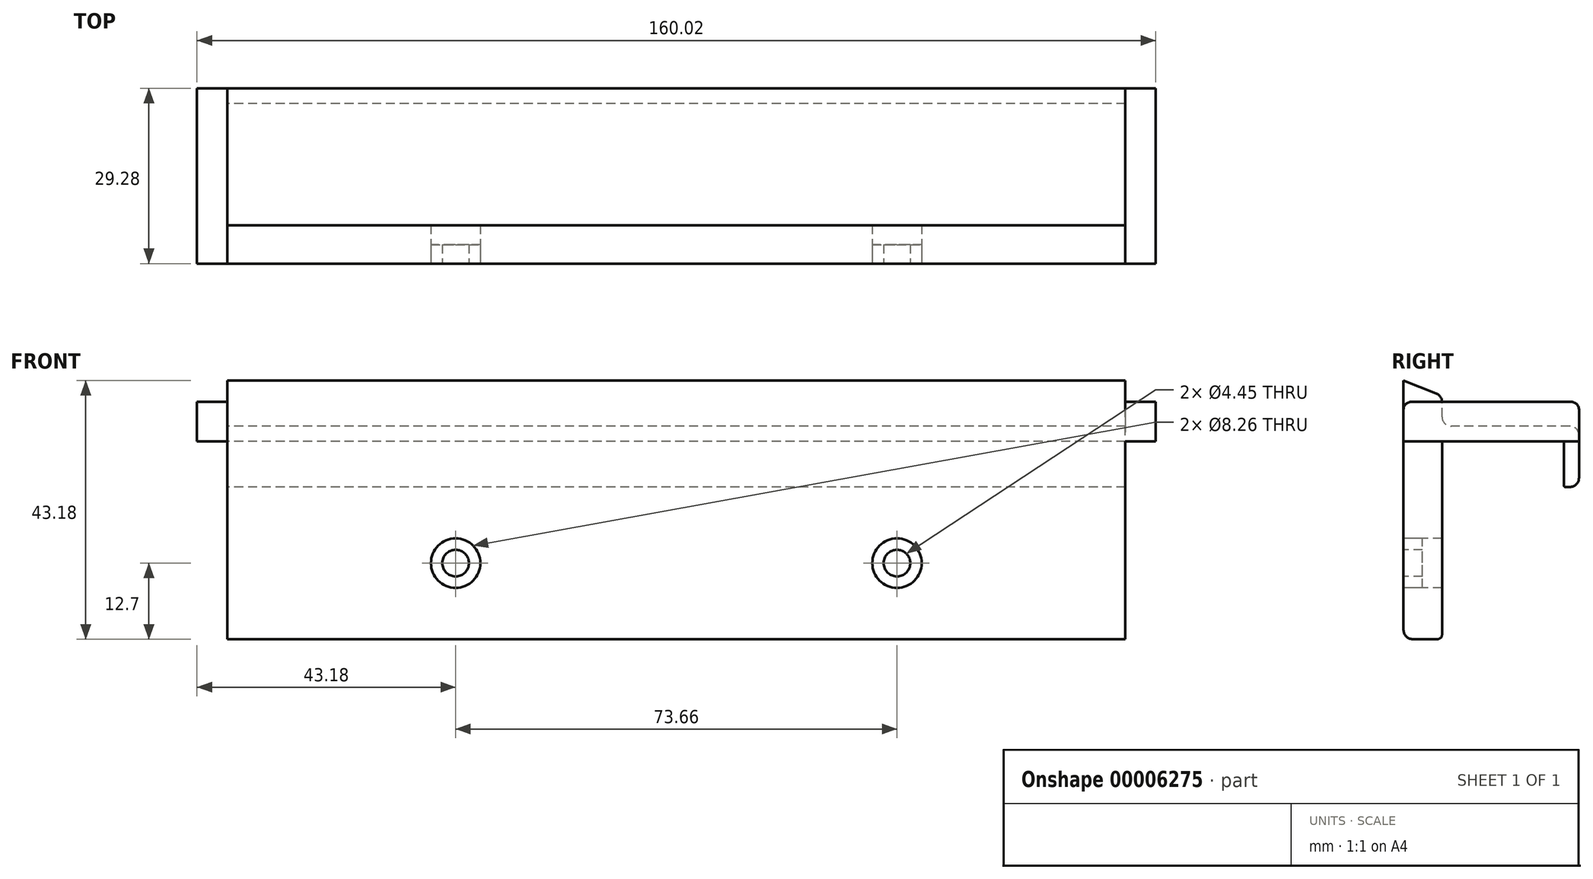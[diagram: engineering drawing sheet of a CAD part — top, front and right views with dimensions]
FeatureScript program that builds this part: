
annotation { "Feature Type Name" : "Feature", "Feature Type Description" : "" }
export const myFeature = defineFeature(function(context is Context, id is Id, definition is map)
    precondition{}
    {
        {
            var Q0;
            Q0=qCreatedBy(makeId("Right.planeOp"),FACE);
            var sketch = newSketch(context, id + "F0", { "sketchPlane" : qUnion([Q0])});
            skLineSegment(sketch, "E0", {"start": v(0.25, 0) * mm, "end": v(20.07, 0) * mm});
            skLineSegment(sketch, "E1", {"start": v(20.32, -0.25) * mm, "end": v(20.32, -7.37) * mm});
            skLineSegment(sketch, "E2", {"start": v(20.57, -7.62) * mm, "end": v(21.34, -7.62) * mm});
            skLineSegment(sketch, "E3", {"start": v(22.86, -6.1) * mm, "end": v(22.86, 1.02) * mm});
            skLineSegment(sketch, "E4", {"start": v(21.34, 2.54) * mm, "end": v(1.52, 2.54) * mm});
            skLineSegment(sketch, "E5", {"start": v(0, 4.06) * mm, "end": v(0, 6.58) * mm});
            skLineSegment(sketch, "E6", {"start": v(-0.96, 8) * mm, "end": v(-6.42, 10.16) * mm});
            skLineSegment(sketch, "E7", {"start": v(-6.42, 10.16) * mm, "end": v(-6.42, -31.5) * mm});
            skLineSegment(sketch, "E8", {"start": v(-4.9, -33.02) * mm, "end": v(-0.76, -33.02) * mm});
            skLineSegment(sketch, "E9", {"start": v(0, -32.26) * mm, "end": v(0, -0.25) * mm});
            skPoint(sketch, "E10.visualSharp", {"position": v(0, 2.54) * mm});
            skArc(sketch, "E10.filletArc", {"start": v(0, 4.06) * mm, "mid": v(0.45, 2.99) * mm, "end": v(1.52, 2.54) * mm});
            skPoint(sketch, "E11.visualSharp", {"position": v(0, 7.62) * mm});
            skArc(sketch, "E11.filletArc", {"start": v(0, 6.58) * mm, "mid": v(-0.26, 7.44) * mm, "end": v(-0.96, 8) * mm});
            skPoint(sketch, "E12.visualSharp", {"position": v(22.86, 2.54) * mm});
            skArc(sketch, "E12.filletArc", {"start": v(22.86, 1.02) * mm, "mid": v(22.41, 2.1) * mm, "end": v(21.34, 2.54) * mm});
            skPoint(sketch, "E13.visualSharp", {"position": v(22.86, -7.62) * mm});
            skArc(sketch, "E13.filletArc", {"start": v(21.34, -7.62) * mm, "mid": v(22.41, -7.17) * mm, "end": v(22.86, -6.1) * mm});
            skPoint(sketch, "E14.visualSharp", {"position": v(-6.42, -33.02) * mm});
            skArc(sketch, "E14.filletArc", {"start": v(-6.42, -31.5) * mm, "mid": v(-5.98, -32.57) * mm, "end": v(-4.9, -33.02) * mm});
            skPoint(sketch, "E15.visualSharp", {"position": v(0, -33.02) * mm});
            skArc(sketch, "E15.filletArc", {"start": v(-0.76, -33.02) * mm, "mid": v(-0.22, -32.8) * mm, "end": v(0, -32.26) * mm});
            skPoint(sketch, "E16.visualSharp", {"position": v(0, 0) * mm});
            skArc(sketch, "E16.filletArc", {"start": v(0.25, 0) * mm, "mid": v(0.07, -0.07) * mm, "end": v(0, -0.25) * mm});
            skPoint(sketch, "E17.visualSharp", {"position": v(20.32, 0) * mm});
            skArc(sketch, "E17.filletArc", {"start": v(20.32, -0.25) * mm, "mid": v(20.25, -0.07) * mm, "end": v(20.07, 0) * mm});
            skPoint(sketch, "E18.visualSharp", {"position": v(20.32, -7.62) * mm});
            skArc(sketch, "E18.filletArc", {"start": v(20.32, -7.37) * mm, "mid": v(20.4, -7.55) * mm, "end": v(20.57, -7.62) * mm});
            skSolve(sketch);
        }
        {
            var Q0;
            Q0=makeQuery(id+"F0.imprint","IMPRINT",FACE,{"disambiguationData":[TD([[makeQuery(id+"F0.imprint","IMPRINT",EDGE,{"derivedFrom":sQuery(id+"F0.wireOp",EDGE,"E0")}),1.0]])]});
            extrude(context, id + "F1", {"entities" : qUnion([Q0]), "endBound" : BoundingType.SYMMETRIC, "depth" : 149.86 * mm});
        }
        {
            var Q0;
            Q0=makeQuery(id+"F1.opExtrude","SWEPT_FACE",FACE,{"disambiguationData":[OSD([sQuery(id+"F0.wireOp",EDGE,"E7")])]});
            var sketch = newSketch(context, id + "F2", { "sketchPlane" : qUnion([Q0])});
            skCircle(sketch, "E19", {"center": v(-36.83, -20.32) * mm, "radius": 4.13 * mm});
            skCircle(sketch, "E20", {"center": v(36.83, -20.32) * mm, "radius": 4.13 * mm});
            skSolve(sketch);
        }
        {
            var Q0;
            Q0=qSketchRegion(id+"F2",true);
            extrude(context, id + "F3", {"entities" : qUnion([Q0]), "operationType" : NewBodyOperationType.REMOVE, "endBound" : BoundingType.UP_TO_NEXT, "oppositeDirection" : true, "depth" : 25.4 * mm});
        }
        {
            var Q0;
            Q0=makeQuery(id+"F1.opExtrude","SWEPT_FACE",FACE,{"disambiguationData":[OSD([sQuery(id+"F0.wireOp",EDGE,"E7")])]});
            var sketch = newSketch(context, id + "F4", { "sketchPlane" : qUnion([Q0])});
            skCircle(sketch, "E21", {"center": v(-36.83, -20.32) * mm, "radius": 2.22 * mm});
            skCircle(sketch, "E22", {"center": v(36.83, -20.32) * mm, "radius": 2.22 * mm});
            skSolve(sketch);
        }
        {
            var Q0;
            Q0=makeQuery(id+"F4.imprint","IMPRINT",FACE,{"disambiguationData":[TD([[makeQuery(id+"F4.imprint","IMPRINT",EDGE,{"derivedFrom":sQuery(id+"F4.wireOp",EDGE,"E21")}),-1.0]])]});
            var Q1;
            Q1=makeQuery(id+"F4.imprint","IMPRINT",FACE,{"disambiguationData":[TD([[makeQuery(id+"F4.imprint","IMPRINT",EDGE,{"derivedFrom":sQuery(id+"F4.wireOp",EDGE,"E22")}),-1.0]])]});
            extrude(context, id + "F5", {"entities" : qUnion([Q0, Q1]), "oppositeDirection" : true, "depth" : 3.17 * mm});
        }
        {
            var Q0;
            Q0=makeQuery(id+"F1.opExtrude","CAP_FACE",FACE,{"disambiguationData":[OSD([sQuery(id+"F0.wireOp",EDGE,"E0"),sQuery(id+"F0.wireOp",EDGE,"E1"),sQuery(id+"F0.wireOp",EDGE,"E2"),sQuery(id+"F0.wireOp",EDGE,"E3"),sQuery(id+"F0.wireOp",EDGE,"E4"),sQuery(id+"F0.wireOp",EDGE,"E5"),sQuery(id+"F0.wireOp",EDGE,"E6"),sQuery(id+"F0.wireOp",EDGE,"E7"),sQuery(id+"F0.wireOp",EDGE,"E8"),sQuery(id+"F0.wireOp",EDGE,"E9"),sQuery(id+"F0.wireOp",EDGE,"E10.filletArc"),sQuery(id+"F0.wireOp",EDGE,"E11.filletArc"),sQuery(id+"F0.wireOp",EDGE,"E12.filletArc"),sQuery(id+"F0.wireOp",EDGE,"E13.filletArc"),sQuery(id+"F0.wireOp",EDGE,"E14.filletArc"),sQuery(id+"F0.wireOp",EDGE,"E15.filletArc"),sQuery(id+"F0.wireOp",EDGE,"E16.filletArc"),sQuery(id+"F0.wireOp",EDGE,"E17.filletArc"),sQuery(id+"F0.wireOp",EDGE,"E18.filletArc")])],"isStart":true});
            var sketch = newSketch(context, id + "F6", { "sketchPlane" : qUnion([Q0])});
            skLineSegment(sketch, "E23.bottom", {"start": v(0, 0) * mm, "end": v(-22.85, 0) * mm});
            skLineSegment(sketch, "E23.top", {"start": v(0, 6.58) * mm, "end": v(-22.85, 6.58) * mm});
            skLineSegment(sketch, "E23.left", {"start": v(0, 0) * mm, "end": v(0, 6.58) * mm});
            skLineSegment(sketch, "E23.right", {"start": v(-22.85, 0) * mm, "end": v(-22.85, 6.58) * mm});
            skSolve(sketch);
        }
        {
            var Q0;
            Q0=makeQuery(id+"F6.imprint","IMPRINT",FACE,{"disambiguationData":[TD([[makeQuery(id+"F6.imprint","IMPRINT",EDGE,{"derivedFrom":makeQuery(id+"F1.opExtrude","CAP_EDGE",EDGE,{"disambiguationData":[OSD([sQuery(id+"F0.wireOp",EDGE,"E6")])],"isStart":true})}),-1.0]])]});
            var sketch = newSketch(context, id + "F7", { "sketchPlane" : qUnion([Q0])});
            skLineSegment(sketch, "E24.bottom", {"start": v(-22.86, 0) * mm, "end": v(6.4, 0) * mm});
            skLineSegment(sketch, "E24.top", {"start": v(-21.6, 6.58) * mm, "end": v(5.14, 6.58) * mm});
            skLineSegment(sketch, "E24.left", {"start": v(-22.86, 0) * mm, "end": v(-22.86, 5.3) * mm});
            skLineSegment(sketch, "E24.right", {"start": v(6.4, 0) * mm, "end": v(6.4, 5.3) * mm});
            skPoint(sketch, "E25.visualSharp", {"position": v(-22.86, 6.58) * mm});
            skArc(sketch, "E25.filletArc", {"start": v(-21.6, 6.58) * mm, "mid": v(-22.49, 6.2) * mm, "end": v(-22.86, 5.3) * mm});
            skPoint(sketch, "E26.visualSharp", {"position": v(6.4, 6.58) * mm});
            skArc(sketch, "E26.filletArc", {"start": v(6.4, 5.3) * mm, "mid": v(6.04, 6.2) * mm, "end": v(5.14, 6.58) * mm});
            skSolve(sketch);
        }
        {
            var Q0;
            Q0=qSketchRegion(id+"F7",true);
            extrude(context, id + "F8", {"entities" : qUnion([Q0]), "operationType" : NewBodyOperationType.ADD, "depth" : 5.08 * mm});
        }
        {
            var Q0;
            Q0=makeQuery(id+"F1.opExtrude","CAP_FACE",FACE,{"disambiguationData":[OSD([sQuery(id+"F0.wireOp",EDGE,"E0"),sQuery(id+"F0.wireOp",EDGE,"E1"),sQuery(id+"F0.wireOp",EDGE,"E2"),sQuery(id+"F0.wireOp",EDGE,"E3"),sQuery(id+"F0.wireOp",EDGE,"E4"),sQuery(id+"F0.wireOp",EDGE,"E5"),sQuery(id+"F0.wireOp",EDGE,"E6"),sQuery(id+"F0.wireOp",EDGE,"E7"),sQuery(id+"F0.wireOp",EDGE,"E8"),sQuery(id+"F0.wireOp",EDGE,"E9"),sQuery(id+"F0.wireOp",EDGE,"E10.filletArc"),sQuery(id+"F0.wireOp",EDGE,"E11.filletArc"),sQuery(id+"F0.wireOp",EDGE,"E12.filletArc"),sQuery(id+"F0.wireOp",EDGE,"E13.filletArc"),sQuery(id+"F0.wireOp",EDGE,"E14.filletArc"),sQuery(id+"F0.wireOp",EDGE,"E15.filletArc"),sQuery(id+"F0.wireOp",EDGE,"E16.filletArc"),sQuery(id+"F0.wireOp",EDGE,"E17.filletArc"),sQuery(id+"F0.wireOp",EDGE,"E18.filletArc")])],"isStart":false});
            var sketch = newSketch(context, id + "F9", { "sketchPlane" : qUnion([Q0])});
            skLineSegment(sketch, "E27.bottom", {"start": v(-6.42, 0) * mm, "end": v(22.86, 0) * mm});
            skLineSegment(sketch, "E27.top", {"start": v(-5.15, 6.58) * mm, "end": v(21.59, 6.58) * mm});
            skLineSegment(sketch, "E27.left", {"start": v(-6.42, 0) * mm, "end": v(-6.42, 5.31) * mm});
            skLineSegment(sketch, "E27.right", {"start": v(22.86, 0) * mm, "end": v(22.86, 5.31) * mm});
            skArc(sketch, "E28.filletArc", {"start": v(22.86, 5.31) * mm, "mid": v(22.49, 6.21) * mm, "end": v(21.59, 6.58) * mm});
            skPoint(sketch, "E29.visualSharp", {"position": v(-6.42, 6.58) * mm});
            skArc(sketch, "E29.filletArc", {"start": v(-5.15, 6.58) * mm, "mid": v(-6.05, 6.21) * mm, "end": v(-6.42, 5.31) * mm});
            skSolve(sketch);
        }
        {
            var Q0;
            Q0=qSketchRegion(id+"F9",true);
            extrude(context, id + "F10", {"entities" : qUnion([Q0]), "operationType" : NewBodyOperationType.ADD, "depth" : 5.08 * mm});
        }
        {
            var Q0;
            Q0=makeQuery(id+"F10.boolean.opBoolean","MERGE",FACE,{"derivedFrom":[makeQuery(id+"F1.opExtrude","SWEPT_FACE",FACE,{"disambiguationData":[OSD([sQuery(id+"F0.wireOp",EDGE,"E7")])]}),makeQuery(id+"F10.opExtrude","SWEPT_FACE",FACE,{"disambiguationData":[OSD([sQuery(id+"F9.wireOp",EDGE,"E27.left")])]})]});
            var sketch = newSketch(context, id + "F11", { "sketchPlane" : qUnion([Q0])});
            skCircle(sketch, "E30", {"center": v(-73.66, 8.89) * mm, "radius": 1.27 * mm});
            skCircle(sketch, "E31", {"center": v(73.66, 8.89) * mm, "radius": 0.64 * mm});
            skSolve(sketch);
        }
        {
            var Q0;
            Q0=qCreatedBy(makeId("Right.planeOp"),FACE);
            var sketch = newSketch(context, id + "F12", { "sketchPlane" : qUnion([Q0])});
            skCircle(sketch, "E32", {"center": v(-82.62, -27.94) * mm, "radius": 6.35 * mm});
            skSolve(sketch);
        }
        {
            var Q0;
            Q0=sQuery(id+"F11.wireOp",VERTEX,"E30.center");
            var Q1;
            Q1=sQuery(id+"F11.wireOp",VERTEX,"E31.center");
            var Q2;
            Q2=sQuery(id+"F12.wireOp",VERTEX,"E32.center");
            cPlane(context, id + "F13", {"entities" : qUnion([Q0, Q1, Q2]), "cplaneType" : CPlaneType.THREE_POINT, "offset" : 152.4 * mm, "width" : 152.4 * mm, "height" : 152.4 * mm});
        }
        {
            var Q0;
            Q0=sQuery(id+"F6.wireOp",EDGE,"E23.top");
            var Q1;
            Q1=sQuery(id+"F12.wireOp",VERTEX,"E32.center");
            cPlane(context, id + "F14", {"entities" : qUnion([Q0, Q1]), "cplaneType" : CPlaneType.LINE_POINT, "offset" : 152.4 * mm, "width" : 152.4 * mm, "height" : 152.4 * mm});
        }
    });
